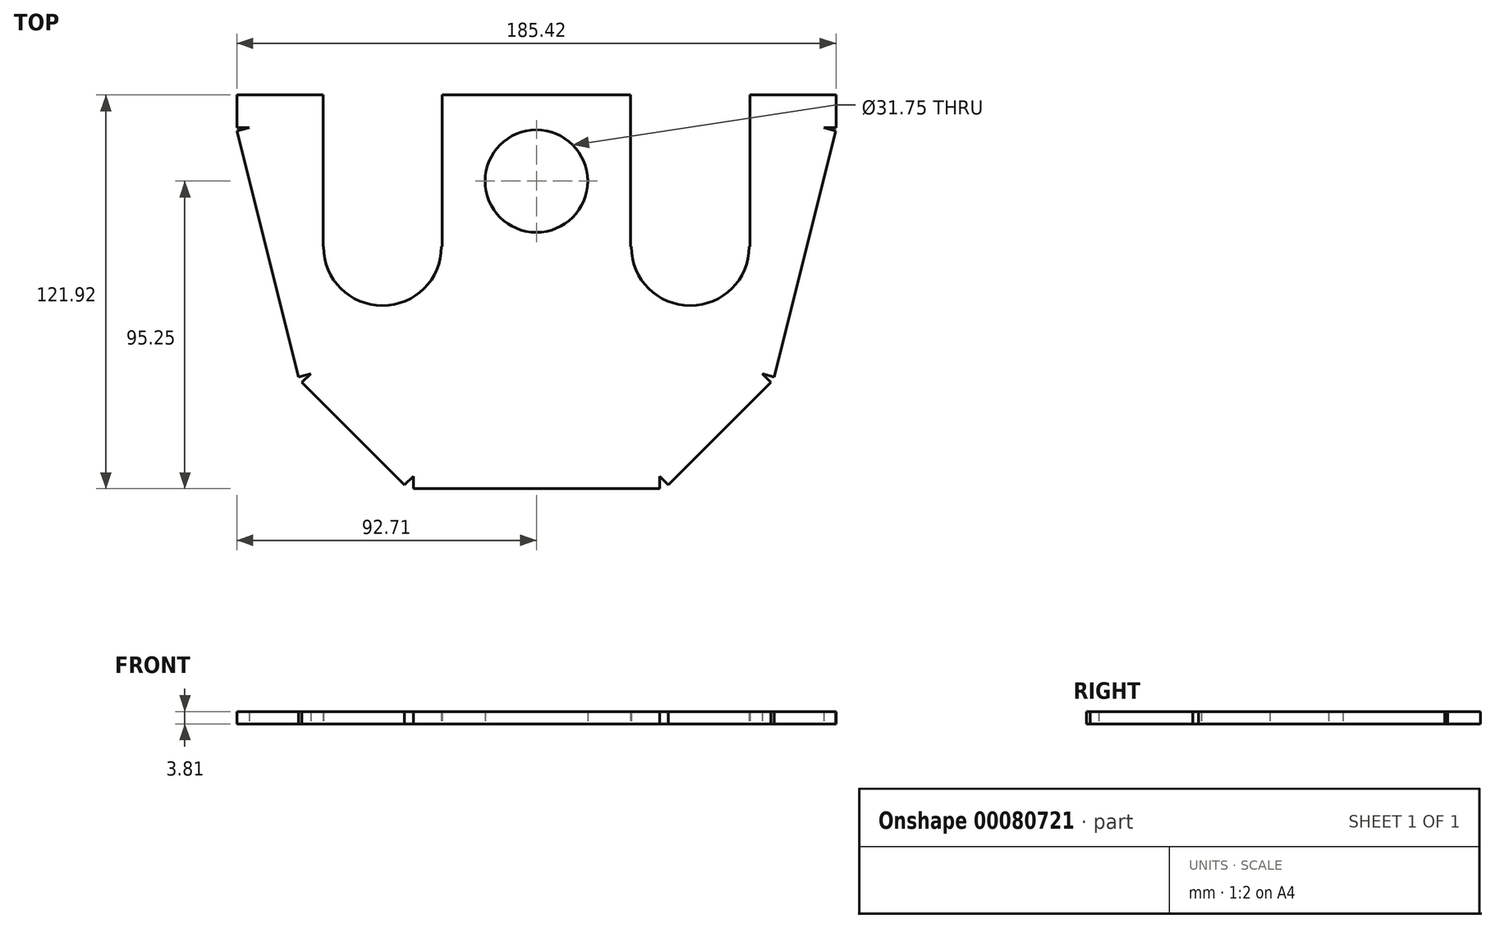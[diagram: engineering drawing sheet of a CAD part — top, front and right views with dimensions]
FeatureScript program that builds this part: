
annotation { "Feature Type Name" : "Feature", "Feature Type Description" : "" }
export const myFeature = defineFeature(function(context is Context, id is Id, definition is map)
    precondition{}
    {
        {
            var Q0;
            Q0=qCreatedBy(makeId("Top.planeOp"),FACE);
            var sketch = newSketch(context, id + "F0", { "sketchPlane" : qUnion([Q0])});
            skLineSegment(sketch, "E0", {"start": v(0, 0) * mm, "end": v(-88.9, 0) * mm, "construction": true});
            skLineSegment(sketch, "E1", {"start": v(0, 0) * mm, "end": v(88.9, 0) * mm, "construction": true});
            skLineSegment(sketch, "E2", {"start": v(-88.9, 50.8) * mm, "end": v(-88.9, 0) * mm});
            skLineSegment(sketch, "E3", {"start": v(88.9, 50.8) * mm, "end": v(88.9, 0) * mm});
            skLineSegment(sketch, "E4", {"start": v(0, -76.2) * mm, "end": v(-69.85, -76.2) * mm, "construction": true});
            skLineSegment(sketch, "E5", {"start": v(0, -76.2) * mm, "end": v(69.85, -76.2) * mm, "construction": true});
            skLineSegment(sketch, "E6", {"start": v(-88.9, 0) * mm, "end": v(-69.85, -76.2) * mm});
            skLineSegment(sketch, "E7", {"start": v(88.9, 0) * mm, "end": v(69.85, -76.2) * mm});
            skLineSegment(sketch, "E8", {"start": v(0, -107.95) * mm, "end": v(-38.1, -107.95) * mm});
            skLineSegment(sketch, "E9", {"start": v(0, -107.95) * mm, "end": v(38.1, -107.95) * mm});
            skLineSegment(sketch, "E10", {"start": v(-69.85, -76.2) * mm, "end": v(-38.1, -107.95) * mm});
            skLineSegment(sketch, "E11", {"start": v(69.85, -76.2) * mm, "end": v(38.1, -107.95) * mm});
            skLineSegment(sketch, "E12.bottom", {"start": v(-29.21, -36.83) * mm, "end": v(-66.04, -36.83) * mm});
            skLineSegment(sketch, "E12.left", {"start": v(-29.21, -36.83) * mm, "end": v(-29.21, 1.27) * mm});
            skLineSegment(sketch, "E12.right", {"start": v(-66.04, -36.83) * mm, "end": v(-66.04, 1.27) * mm});
            skPoint(sketch, "E12.middle", {"position": v(-47.63, -17.78) * mm});
            skLineSegment(sketch, "E13", {"start": v(0, 50.8) * mm, "end": v(0, -107.95) * mm, "construction": true});
            skCircle(sketch, "E14", {"center": v(0, -16.51) * mm, "radius": 15.88 * mm});
            skLineSegment(sketch, "E15", {"start": v(-66.04, 1.27) * mm, "end": v(-66.04, 50.8) * mm});
            skLineSegment(sketch, "E16", {"start": v(-29.21, 1.27) * mm, "end": v(-29.21, 50.8) * mm});
            skLineSegment(sketch, "E17.MirrorCS", {"start": v(29.21, 1.27) * mm, "end": v(29.21, 50.8) * mm});
            skLineSegment(sketch, "E18.MirrorCS", {"start": v(66.04, 1.27) * mm, "end": v(66.04, 50.8) * mm});
            skLineSegment(sketch, "E19.MirrorCS", {"start": v(29.21, -36.83) * mm, "end": v(29.21, 1.27) * mm});
            skLineSegment(sketch, "E20.MirrorCS", {"start": v(66.04, -36.83) * mm, "end": v(66.04, 1.27) * mm});
            skLineSegment(sketch, "E21.MirrorCS", {"start": v(29.21, -36.83) * mm, "end": v(66.04, -36.83) * mm});
            skLineSegment(sketch, "E22", {"start": v(-88.9, 50.8) * mm, "end": v(-66.04, 50.8) * mm});
            skLineSegment(sketch, "E23", {"start": v(-29.21, 50.8) * mm, "end": v(0, 50.8) * mm});
            skLineSegment(sketch, "E24", {"start": v(29.21, 50.8) * mm, "end": v(0, 50.8) * mm});
            skLineSegment(sketch, "E25", {"start": v(66.04, 50.8) * mm, "end": v(88.9, 50.8) * mm});
            skCircle(sketch, "E26", {"center": v(-47.63, -36.83) * mm, "radius": 18.24 * mm});
            skCircle(sketch, "E27.MirrorC", {"center": v(47.63, -36.83) * mm, "radius": 18.24 * mm});
            skSolve(sketch);
        }
        {
            var Q0;
            {var subQ8=sQuery(id+"F0.wireOp",EDGE,"E2");Q0=makeQuery(id+"F0.imprint","IMPRINT",FACE,{"disambiguationData":[TD([[makeQuery(id+"F0.imprint","IMPRINT",EDGE,{"derivedFrom":subQ8}),1.0]])]});}
            extrude(context, id + "F1", {"entities" : qUnion([Q0]), "depth" : 3.8 * mm});
        }
        {
            var Q0;
            Q0=makeQuery(id+"F1.opExtrude","SWEPT_BODY",BODY,{"disambiguationData":[OSD([sQuery(id+"F0.wireOp",EDGE,"zUoSRjR9-PS5d-3Myj-Tx5W-22LiFs0HkAtE"),sQuery(id+"F0.wireOp",EDGE,"MPji2FRN-cKGx-X8EU-Ca2n-P1ynlB2nKAyP"),sQuery(id+"F0.wireOp",EDGE,"E2"),sQuery(id+"F0.wireOp",EDGE,"E3"),sQuery(id+"F0.wireOp",EDGE,"E6"),sQuery(id+"F0.wireOp",EDGE,"E7"),sQuery(id+"F0.wireOp",EDGE,"E8"),sQuery(id+"F0.wireOp",EDGE,"E9"),sQuery(id+"F0.wireOp",EDGE,"E10"),sQuery(id+"F0.wireOp",EDGE,"E11"),sQuery(id+"F0.wireOp",EDGE,"E12.bottom"),sQuery(id+"F0.wireOp",EDGE,"E12.top"),sQuery(id+"F0.wireOp",EDGE,"E12.left"),sQuery(id+"F0.wireOp",EDGE,"E12.right")])]});
            var Q1;
            Q1=qCreatedBy(makeId("Right.planeOp"),FACE);
            mirror(context, id + "F2", {"operationType" : NewBodyOperationType.INTERSECT, "entities" : qUnion([Q0]), "mirrorPlane" : qUnion([Q1])});
        }
        {
            var Q0;
            Q0=makeQuery(id+"F1.opExtrude","SWEPT_FACE",FACE,{"disambiguationData":[OSD([sQuery(id+"F0.wireOp",EDGE,"E23"),sQuery(id+"F0.wireOp",EDGE,"E24")])]});
            var Q1;
            Q1=makeQuery(id+"F1.opExtrude","SWEPT_FACE",FACE,{"disambiguationData":[OSD([sQuery(id+"F0.wireOp",EDGE,"E25")])]});
            var Q2;
            Q2=makeQuery(id+"F1.opExtrude","SWEPT_FACE",FACE,{"disambiguationData":[OSD([sQuery(id+"F0.wireOp",EDGE,"E22")])]});
            extrude(context, id + "F3", {"entities" : qUnion([Q0, Q1, Q2]), "operationType" : NewBodyOperationType.REMOVE, "oppositeDirection" : true, "depth" : 40.64 * mm});
        }
        {
            var Q0;
            Q0=makeQuery(id+"F1.opExtrude","SWEPT_FACE",FACE,{"disambiguationData":[OSD([sQuery(id+"F0.wireOp",EDGE,"E8"),sQuery(id+"F0.wireOp",EDGE,"E9")])]});
            extrude(context, id + "F4", {"entities" : qUnion([Q0]), "operationType" : NewBodyOperationType.ADD, "depth" : 3.8 * mm});
        }
        {
            var Q0;
            Q0=makeQuery(id+"F1.opExtrude","SWEPT_FACE",FACE,{"disambiguationData":[OSD([sQuery(id+"F0.wireOp",EDGE,"E10")])]});
            extrude(context, id + "F5", {"entities" : qUnion([Q0]), "operationType" : NewBodyOperationType.ADD, "depth" : 3.8 * mm});
        }
        {
            var Q0;
            Q0=makeQuery(id+"F1.opExtrude","SWEPT_FACE",FACE,{"disambiguationData":[OSD([sQuery(id+"F0.wireOp",EDGE,"E6")])]});
            extrude(context, id + "F6", {"entities" : qUnion([Q0]), "operationType" : NewBodyOperationType.ADD, "depth" : 3.8 * mm});
        }
        {
            var Q0;
            Q0=makeQuery(id+"F1.opExtrude","SWEPT_FACE",FACE,{"disambiguationData":[OSD([sQuery(id+"F0.wireOp",EDGE,"E2")])]});
            extrude(context, id + "F7", {"entities" : qUnion([Q0]), "operationType" : NewBodyOperationType.ADD, "depth" : 3.8 * mm});
        }
        {
            var Q0;
            Q0=makeQuery(id+"F1.opExtrude","SWEPT_FACE",FACE,{"disambiguationData":[OSD([sQuery(id+"F0.wireOp",EDGE,"E11")])]});
            extrude(context, id + "F8", {"entities" : qUnion([Q0]), "operationType" : NewBodyOperationType.ADD, "depth" : 3.8 * mm});
        }
        {
            var Q0;
            Q0=makeQuery(id+"F1.opExtrude","SWEPT_FACE",FACE,{"disambiguationData":[OSD([sQuery(id+"F0.wireOp",EDGE,"E7")])]});
            extrude(context, id + "F9", {"entities" : qUnion([Q0]), "operationType" : NewBodyOperationType.ADD, "depth" : 3.8 * mm});
        }
        {
            var Q0;
            Q0=makeQuery(id+"F1.opExtrude","SWEPT_FACE",FACE,{"disambiguationData":[OSD([sQuery(id+"F0.wireOp",EDGE,"E3")])]});
            extrude(context, id + "F10", {"entities" : qUnion([Q0]), "operationType" : NewBodyOperationType.ADD, "depth" : 3.8 * mm});
        }
    });
